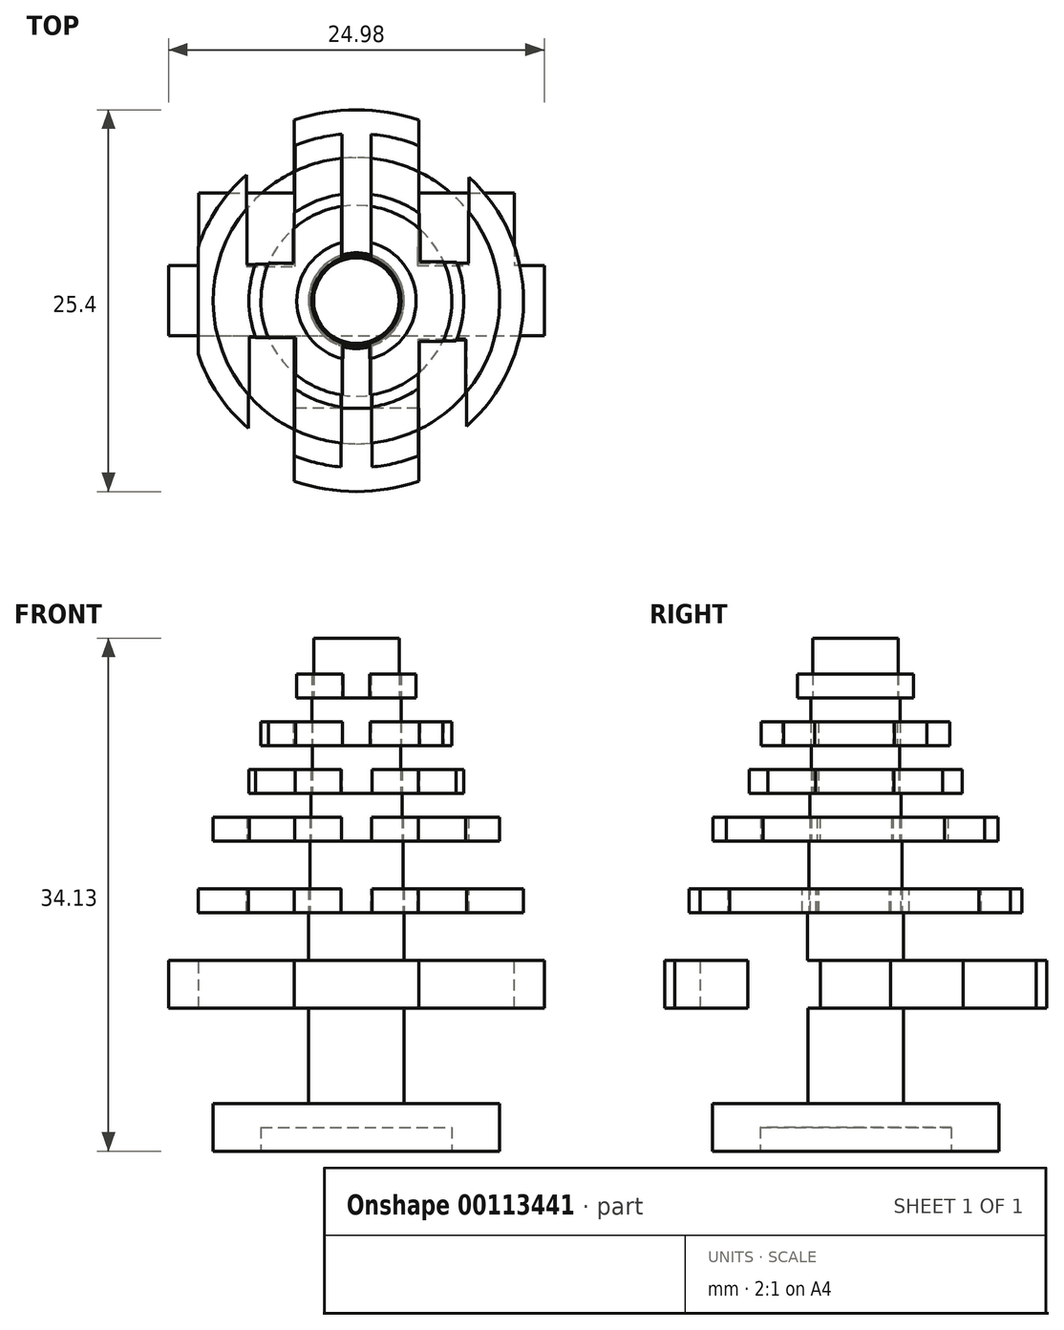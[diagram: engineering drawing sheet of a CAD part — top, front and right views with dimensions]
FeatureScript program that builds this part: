
annotation { "Feature Type Name" : "Feature", "Feature Type Description" : "" }
export const myFeature = defineFeature(function(context is Context, id is Id, definition is map)
    precondition{}
    {
        {
            var Q0;
            Q0=qCreatedBy(makeId("Top.planeOp"),FACE);
            var sketch = newSketch(context, id + "F0", { "sketchPlane" : qUnion([Q0])});
            skCircle(sketch, "E0", {"center": v(0, 0) * mm, "radius": 9.53 * mm});
            skSolve(sketch);
        }
        {
            var Q0;
            Q0=makeQuery(id+"F0.imprint","IMPRINT",FACE,{"disambiguationData":[TD([[makeQuery(id+"F0.imprint","IMPRINT",EDGE,{"derivedFrom":sQuery(id+"F0.wireOp",EDGE,"E0")}),1.0]])]});
            extrude(context, id + "F1", {"entities" : qUnion([Q0]), "depth" : 3.17 * mm});
        }
        {
            var Q0;
            Q0=makeQuery(id+"F1.opExtrude","CAP_FACE",FACE,{"disambiguationData":[OSD([sQuery(id+"F0.wireOp",EDGE,"E0")])],"isStart":false});
            var sketch = newSketch(context, id + "F2", { "sketchPlane" : qUnion([Q0])});
            skCircle(sketch, "E1", {"center": v(0, 0) * mm, "radius": 3.18 * mm});
            skSolve(sketch);
        }
        {
            var Q0;
            Q0=makeQuery(id+"F2.imprint","IMPRINT",FACE,{"disambiguationData":[TD([[makeQuery(id+"F2.imprint","IMPRINT",EDGE,{"derivedFrom":sQuery(id+"F2.wireOp",EDGE,"E1")}),1.0]])]});
            extrude(context, id + "F3", {"entities" : qUnion([Q0]), "depth" : 6.35 * mm});
        }
        {
            var Q0;
            Q0=makeQuery(id+"F1.opExtrude","CAP_FACE",FACE,{"disambiguationData":[OSD([sQuery(id+"F0.wireOp",EDGE,"E0")])],"isStart":true});
            var sketch = newSketch(context, id + "F4", { "sketchPlane" : qUnion([Q0])});
            skCircle(sketch, "E2", {"center": v(0, 0) * mm, "radius": 6.35 * mm});
            skSolve(sketch);
        }
        {
            var Q0;
            Q0=makeQuery(id+"F3.opExtrude","CAP_FACE",FACE,{"disambiguationData":[OSD([sQuery(id+"F2.wireOp",EDGE,"E1")])],"isStart":false});
            var sketch = newSketch(context, id + "F5", { "sketchPlane" : qUnion([Q0])});
            skCircle(sketch, "E3", {"center": v(0, 0) * mm, "radius": 12.7 * mm});
            skSolve(sketch);
        }
        {
            var Q0;
            Q0=makeQuery(id+"F5.imprint","IMPRINT",FACE,{"disambiguationData":[TD([[makeQuery(id+"F5.imprint","IMPRINT",EDGE,{"derivedFrom":makeQuery(id+"F3.opExtrude","CAP_EDGE",EDGE,{"disambiguationData":[OSD([sQuery(id+"F2.wireOp",EDGE,"E1")])],"isStart":false})}),1.0]])]});
            var Q1;
            Q1=makeQuery(id+"F5.imprint","IMPRINT",FACE,{"disambiguationData":[TD([[makeQuery(id+"F5.imprint","IMPRINT",EDGE,{"derivedFrom":sQuery(id+"F5.wireOp",EDGE,"E3")}),1.0]])]});
            extrude(context, id + "F6", {"entities" : qUnion([Q0, Q1]), "operationType" : NewBodyOperationType.ADD, "depth" : 3.17 * mm});
        }
        {
            var Q0;
            Q0=makeQuery(id+"F6.opExtrude","CAP_FACE",FACE,{"disambiguationData":[OSD([sQuery(id+"F5.wireOp",EDGE,"E3")])],"isStart":false});
            var sketch = newSketch(context, id + "F7", { "sketchPlane" : qUnion([Q0])});
            skLineSegment(sketch, "E4", {"start": v(10.49, 7.16) * mm, "end": v(10.49, -7.16) * mm});
            skLineSegment(sketch, "E5", {"start": v(10.49, -2.32) * mm, "end": v(12.49, -2.32) * mm});
            skLineSegment(sketch, "E6", {"start": v(12.49, -2.32) * mm, "end": v(12.49, 2.32) * mm});
            skLineSegment(sketch, "E7", {"start": v(12.49, 2.32) * mm, "end": v(10.49, 2.32) * mm});
            skLineSegment(sketch, "E8", {"start": v(10.49, 2.32) * mm, "end": v(-12.49, 2.32) * mm});
            skLineSegment(sketch, "E9", {"start": v(-12.49, 2.32) * mm, "end": v(-12.49, -2.32) * mm});
            skLineSegment(sketch, "E10", {"start": v(-12.49, -2.32) * mm, "end": v(10.49, -2.32) * mm});
            skLineSegment(sketch, "E11", {"start": v(10.49, -7.16) * mm, "end": v(-10.49, -7.16) * mm});
            skLineSegment(sketch, "E12", {"start": v(-10.49, -7.16) * mm, "end": v(-10.49, 7.16) * mm});
            skLineSegment(sketch, "E13", {"start": v(-10.49, 7.16) * mm, "end": v(10.49, 7.16) * mm});
            skLineSegment(sketch, "E14", {"start": v(-10.49, 2.32) * mm, "end": v(-12.49, 2.32) * mm});
            skLineSegment(sketch, "E15", {"start": v(-10.49, 7.16) * mm, "end": v(-7.31, 7.16) * mm});
            skLineSegment(sketch, "E16", {"start": v(-7.31, 7.16) * mm, "end": v(-7.31, 10.38) * mm});
            skLineSegment(sketch, "E17", {"start": v(-4.14, 12) * mm, "end": v(-4.14, 7.16) * mm});
            skLineSegment(sketch, "E18", {"start": v(-7.31, 7.16) * mm, "end": v(-4.14, 7.16) * mm});
            skLineSegment(sketch, "E19", {"start": v(10.49, 7.16) * mm, "end": v(7.31, 7.16) * mm});
            skLineSegment(sketch, "E20", {"start": v(7.31, 7.16) * mm, "end": v(7.31, 10.38) * mm});
            skLineSegment(sketch, "E21", {"start": v(7.31, 7.16) * mm, "end": v(4.14, 7.16) * mm});
            skLineSegment(sketch, "E22", {"start": v(4.14, 7.16) * mm, "end": v(4.14, 12) * mm});
            skLineSegment(sketch, "E23", {"start": v(-4.14, 7.16) * mm, "end": v(-0.96, 7.16) * mm});
            skLineSegment(sketch, "E24", {"start": v(-0.96, 7.16) * mm, "end": v(-0.96, 12.66) * mm});
            skLineSegment(sketch, "E25", {"start": v(4.14, 7.16) * mm, "end": v(0.96, 7.16) * mm});
            skLineSegment(sketch, "E26", {"start": v(0.96, 7.16) * mm, "end": v(0.96, 12.66) * mm});
            skLineSegment(sketch, "E27", {"start": v(-10.49, -7.16) * mm, "end": v(-7.31, -7.16) * mm});
            skLineSegment(sketch, "E28", {"start": v(-7.31, -7.16) * mm, "end": v(-7.31, -10.38) * mm});
            skLineSegment(sketch, "E29", {"start": v(-7.31, -7.16) * mm, "end": v(-4.14, -7.16) * mm});
            skLineSegment(sketch, "E30", {"start": v(-4.14, -7.16) * mm, "end": v(-4.14, -12) * mm});
            skLineSegment(sketch, "E31", {"start": v(-4.14, -7.16) * mm, "end": v(-0.96, -7.16) * mm});
            skLineSegment(sketch, "E32", {"start": v(-0.96, -7.16) * mm, "end": v(-0.96, -12.66) * mm});
            skLineSegment(sketch, "E33", {"start": v(10.49, -7.16) * mm, "end": v(7.31, -7.16) * mm});
            skLineSegment(sketch, "E34", {"start": v(7.31, -7.16) * mm, "end": v(7.31, -10.38) * mm});
            skLineSegment(sketch, "E35", {"start": v(7.31, -7.16) * mm, "end": v(4.14, -7.16) * mm});
            skLineSegment(sketch, "E36", {"start": v(4.14, -7.16) * mm, "end": v(4.14, -12) * mm});
            skLineSegment(sketch, "E37", {"start": v(4.14, -7.16) * mm, "end": v(0.96, -7.16) * mm});
            skLineSegment(sketch, "E38", {"start": v(0.96, -7.16) * mm, "end": v(0.96, -12.66) * mm});
            skLineSegment(sketch, "E39", {"start": v(-0.96, 7.16) * mm, "end": v(-0.96, 2.32) * mm});
            skLineSegment(sketch, "E40", {"start": v(-0.96, 2.32) * mm, "end": v(-4.14, 2.32) * mm});
            skLineSegment(sketch, "E41", {"start": v(-4.14, 2.32) * mm, "end": v(-4.14, 7.16) * mm});
            skLineSegment(sketch, "E42", {"start": v(-4.14, 2.32) * mm, "end": v(-7.31, 2.32) * mm});
            skLineSegment(sketch, "E43", {"start": v(-7.31, 2.32) * mm, "end": v(-7.31, 7.16) * mm});
            skLineSegment(sketch, "E44", {"start": v(-7.31, 2.32) * mm, "end": v(-10.49, 2.32) * mm});
            skLineSegment(sketch, "E45", {"start": v(0.96, 7.16) * mm, "end": v(0.96, 2.32) * mm});
            skLineSegment(sketch, "E46", {"start": v(0.96, 2.32) * mm, "end": v(4.14, 2.32) * mm});
            skLineSegment(sketch, "E47", {"start": v(4.14, 2.32) * mm, "end": v(4.14, 7.16) * mm});
            skLineSegment(sketch, "E48", {"start": v(4.14, 2.32) * mm, "end": v(7.31, 2.32) * mm});
            skLineSegment(sketch, "E49", {"start": v(7.31, 2.32) * mm, "end": v(7.31, 7.16) * mm});
            skLineSegment(sketch, "E50", {"start": v(7.31, 2.32) * mm, "end": v(10.49, 2.32) * mm});
            skLineSegment(sketch, "E51", {"start": v(7.31, -7.16) * mm, "end": v(7.31, -2.32) * mm});
            skLineSegment(sketch, "E52", {"start": v(4.14, -7.16) * mm, "end": v(4.14, -2.32) * mm});
            skLineSegment(sketch, "E53", {"start": v(0.96, -7.16) * mm, "end": v(0.96, -2.32) * mm});
            skLineSegment(sketch, "E54", {"start": v(-0.96, -7.16) * mm, "end": v(-0.96, -2.32) * mm});
            skLineSegment(sketch, "E55", {"start": v(-4.14, -7.16) * mm, "end": v(-4.14, -2.32) * mm});
            skLineSegment(sketch, "E56", {"start": v(-7.31, -7.16) * mm, "end": v(-7.31, -2.32) * mm});
            skSolve(sketch);
        }
        {
            var Q0;
            {var subQ1=sQuery(id+"F7.wireOp",EDGE,"E9");Q0=makeQuery(id+"F7.imprint","IMPRINT",FACE,{"disambiguationData":[TD([[makeQuery(id+"F7.imprint","IMPRINT",EDGE,{"derivedFrom":subQ1}),-1.0]])]});}
            var Q1;
            {var subQ3=sQuery(id+"F7.wireOp",EDGE,"E14");Q1=makeQuery(id+"F7.imprint","IMPRINT",FACE,{"disambiguationData":[TD([[makeQuery(id+"F7.imprint","IMPRINT",EDGE,{"derivedFrom":subQ3}),-1.0]])]});}
            var Q2;
            {var subQ1=sQuery(id+"F7.wireOp",EDGE,"E12");var subQ3=sQuery(id+"F7.wireOp",EDGE,"E10");var subQ5=makeQuery(id+"F7.imprint","INTERSECT",VERTEX,{"derivedFrom":[subQ3,subQ1]});Q2=makeQuery(id+"F7.imprint","IMPRINT",FACE,{"disambiguationData":[TD([[makeQuery(id+"F7.imprint","IMPRINT",EDGE,{"disambiguationData":[TD([[subQ5,1.0]])],"derivedFrom":subQ3}),-1.0]])]});}
            var Q3;
            {var subQ2=sQuery(id+"F7.wireOp",EDGE,"E28");Q3=makeQuery(id+"F7.imprint","IMPRINT",FACE,{"disambiguationData":[TD([[makeQuery(id+"F7.imprint","IMPRINT",EDGE,{"derivedFrom":subQ2}),1.0]])]});}
            var Q4;
            Q4=makeQuery(id+"F7.imprint","IMPRINT",FACE,{"disambiguationData":[TD([[makeQuery(id+"F7.imprint","IMPRINT",EDGE,{"derivedFrom":sQuery(id+"F7.wireOp",EDGE,"E29")}),1.0]])]});
            var Q5;
            Q5=makeQuery(id+"F7.imprint","IMPRINT",FACE,{"disambiguationData":[TD([[makeQuery(id+"F7.imprint","IMPRINT",EDGE,{"derivedFrom":sQuery(id+"F7.wireOp",EDGE,"E18")}),-1.0]])]});
            var Q6;
            {var subQ2=sQuery(id+"F7.wireOp",EDGE,"E16");Q6=makeQuery(id+"F7.imprint","IMPRINT",FACE,{"disambiguationData":[TD([[makeQuery(id+"F7.imprint","IMPRINT",EDGE,{"derivedFrom":subQ2}),-1.0]])]});}
            var Q7;
            Q7=makeQuery(id+"F7.imprint","IMPRINT",FACE,{"disambiguationData":[TD([[makeQuery(id+"F7.imprint","IMPRINT",EDGE,{"derivedFrom":sQuery(id+"F7.wireOp",EDGE,"E13")}),1.0]])]});
            var Q8;
            Q8=makeQuery(id+"F7.imprint","IMPRINT",FACE,{"disambiguationData":[TD([[makeQuery(id+"F7.imprint","IMPRINT",EDGE,{"derivedFrom":sQuery(id+"F7.wireOp",EDGE,"E8")}),-1.0]])]});
            var Q9;
            Q9=makeQuery(id+"F7.imprint","IMPRINT",FACE,{"disambiguationData":[TD([[makeQuery(id+"F7.imprint","IMPRINT",EDGE,{"derivedFrom":sQuery(id+"F7.wireOp",EDGE,"E11")}),-1.0]])]});
            var Q10;
            Q10=makeQuery(id+"F7.imprint","IMPRINT",FACE,{"disambiguationData":[TD([[makeQuery(id+"F7.imprint","IMPRINT",EDGE,{"derivedFrom":sQuery(id+"F7.wireOp",EDGE,"E11")}),1.0]])]});
            var Q11;
            {var subQ2=sQuery(id+"F7.wireOp",EDGE,"E34");Q11=makeQuery(id+"F7.imprint","IMPRINT",FACE,{"disambiguationData":[TD([[makeQuery(id+"F7.imprint","IMPRINT",EDGE,{"derivedFrom":subQ2}),-1.0]])]});}
            var Q12;
            Q12=makeQuery(id+"F7.imprint","IMPRINT",FACE,{"disambiguationData":[TD([[makeQuery(id+"F7.imprint","IMPRINT",EDGE,{"derivedFrom":sQuery(id+"F7.wireOp",EDGE,"E35")}),-1.0]])]});
            var Q13;
            {var subQ1=sQuery(id+"F7.wireOp",EDGE,"E5");Q13=makeQuery(id+"F7.imprint","IMPRINT",FACE,{"disambiguationData":[TD([[makeQuery(id+"F7.imprint","IMPRINT",EDGE,{"derivedFrom":subQ1}),-1.0]])]});}
            var Q14;
            {var subQ0=sQuery(id+"F7.wireOp",EDGE,"E7");Q14=makeQuery(id+"F7.imprint","IMPRINT",FACE,{"disambiguationData":[TD([[makeQuery(id+"F7.imprint","IMPRINT",EDGE,{"derivedFrom":subQ0}),-1.0]])]});}
            var Q15;
            Q15=makeQuery(id+"F7.imprint","IMPRINT",FACE,{"disambiguationData":[TD([[makeQuery(id+"F7.imprint","IMPRINT",EDGE,{"derivedFrom":sQuery(id+"F7.wireOp",EDGE,"E21")}),1.0]])]});
            var Q16;
            {var subQ2=sQuery(id+"F7.wireOp",EDGE,"E20");Q16=makeQuery(id+"F7.imprint","IMPRINT",FACE,{"disambiguationData":[TD([[makeQuery(id+"F7.imprint","IMPRINT",EDGE,{"derivedFrom":subQ2}),1.0]])]});}
            var Q17;
            {var subQ1=sQuery(id+"F7.wireOp",EDGE,"E6");Q17=makeQuery(id+"F7.imprint","IMPRINT",FACE,{"disambiguationData":[TD([[makeQuery(id+"F7.imprint","IMPRINT",EDGE,{"derivedFrom":subQ1}),-1.0]])]});}
            extrude(context, id + "F8", {"entities" : qUnion([Q0, Q1, Q2, Q3, Q4, Q5, Q6, Q7, Q8, Q9, Q10, Q11, Q12, Q13, Q14, Q15, Q16, Q17]), "operationType" : NewBodyOperationType.REMOVE, "oppositeDirection" : true, "depth" : 3.17 * mm});
        }
        {
            var Q0;
            Q0=makeQuery(id+"F7.imprint","IMPRINT",FACE,{"disambiguationData":[TD([[makeQuery(id+"F7.imprint","IMPRINT",EDGE,{"derivedFrom":sQuery(id+"F7.wireOp",EDGE,"E8")}),1.0]])]});
            var sketch = newSketch(context, id + "F9", { "sketchPlane" : qUnion([Q0])});
            skCircle(sketch, "E57", {"center": v(0, 0) * mm, "radius": 3.18 * mm});
            skSolve(sketch);
        }
        {
            var Q0;
            Q0=qSketchRegion(id+"F9",true);
            extrude(context, id + "F10", {"entities" : qUnion([Q0]), "operationType" : NewBodyOperationType.ADD, "depth" : 3.17 * mm});
        }
        {
            var Q0;
            Q0=makeQuery(id+"F10.opExtrude","CAP_FACE",FACE,{"disambiguationData":[OSD([sQuery(id+"F9.wireOp",EDGE,"E57")])],"isStart":false});
            var sketch = newSketch(context, id + "F11", { "sketchPlane" : qUnion([Q0])});
            skCircle(sketch, "E58", {"center": v(0, 0) * mm, "radius": 11.11 * mm});
            skSolve(sketch);
        }
        {
            var Q0;
            Q0=makeQuery(id+"F11.imprint","IMPRINT",FACE,{"disambiguationData":[TD([[makeQuery(id+"F11.imprint","IMPRINT",EDGE,{"derivedFrom":sQuery(id+"F11.wireOp",EDGE,"E58")}),1.0]])]});
            extrude(context, id + "F12", {"entities" : qUnion([Q0]), "depth" : 1.59 * mm});
        }
        {
            var Q0;
            Q0=makeQuery(id+"F12.opExtrude","CAP_FACE",FACE,{"disambiguationData":[OSD([sQuery(id+"F9.wireOp",EDGE,"E57"),sQuery(id+"F11.wireOp",EDGE,"E58")])],"isStart":false});
            var sketch = newSketch(context, id + "F13", { "sketchPlane" : qUnion([Q0])});
            skLineSegment(sketch, "E59", {"start": v(-0.97, 3.03) * mm, "end": v(-0.97, 11.07) * mm});
            skLineSegment(sketch, "E60", {"start": v(-0.97, 11.07) * mm, "end": v(0.97, 11.07) * mm});
            skLineSegment(sketch, "E61", {"start": v(0.97, 11.07) * mm, "end": v(0.97, 3.03) * mm});
            skLineSegment(sketch, "E62", {"start": v(0.97, 3.03) * mm, "end": v(-0.97, 3.03) * mm});
            skLineSegment(sketch, "E63", {"start": v(4.06, 2.35) * mm, "end": v(7.5, 2.35) * mm});
            skLineSegment(sketch, "E64", {"start": v(7.5, 2.35) * mm, "end": v(7.5, 8.2) * mm});
            skLineSegment(sketch, "E65", {"start": v(7.5, 8.2) * mm, "end": v(4.16, 10.3) * mm});
            skLineSegment(sketch, "E66", {"start": v(4.16, 10.3) * mm, "end": v(4.06, 2.35) * mm});
            skLineSegment(sketch, "E67", {"start": v(10.59, 3.37) * mm, "end": v(10.59, -3.37) * mm});
            skLineSegment(sketch, "E68", {"start": v(-10.53, 3.55) * mm, "end": v(-10.53, -3.55) * mm});
            skLineSegment(sketch, "E69", {"start": v(-7.31, 8.37) * mm, "end": v(-7.31, 2.26) * mm});
            skLineSegment(sketch, "E70", {"start": v(-7.31, 2.26) * mm, "end": v(-4.08, 2.26) * mm});
            skLineSegment(sketch, "E71", {"start": v(-4.08, 2.26) * mm, "end": v(-4.08, 10.34) * mm});
            skLineSegment(sketch, "E72", {"start": v(-4.08, 10.34) * mm, "end": v(-7.31, 8.37) * mm});
            skLineSegment(sketch, "E73", {"start": v(-7.17, -2.44) * mm, "end": v(-7.17, -8.49) * mm});
            skLineSegment(sketch, "E74", {"start": v(-7.17, -8.49) * mm, "end": v(-4.13, -10.32) * mm});
            skLineSegment(sketch, "E75", {"start": v(-4.13, -10.32) * mm, "end": v(-4.13, -2.48) * mm});
            skLineSegment(sketch, "E76", {"start": v(-4.13, -2.48) * mm, "end": v(-7.17, -2.44) * mm});
            skLineSegment(sketch, "E77", {"start": v(-1.04, -2.53) * mm, "end": v(-1.04, -11.06) * mm});
            skLineSegment(sketch, "E78", {"start": v(-1.04, -11.06) * mm, "end": v(1.04, -11.06) * mm});
            skLineSegment(sketch, "E79", {"start": v(1.04, -11.06) * mm, "end": v(1.04, -3) * mm});
            skLineSegment(sketch, "E80", {"start": v(1.04, -3) * mm, "end": v(-1.04, -3) * mm});
            skLineSegment(sketch, "E81", {"start": v(4.11, -10.32) * mm, "end": v(4.11, -2.61) * mm});
            skLineSegment(sketch, "E82", {"start": v(4.11, -2.61) * mm, "end": v(7.32, -2.61) * mm});
            skLineSegment(sketch, "E83", {"start": v(7.32, -2.61) * mm, "end": v(7.32, -8.36) * mm});
            skLineSegment(sketch, "E84", {"start": v(7.32, -8.36) * mm, "end": v(4.11, -10.32) * mm});
            skSolve(sketch);
        }
        {
            var Q0;
            {var subQ1=sQuery(id+"F13.wireOp",EDGE,"E78");Q0=makeQuery(id+"F13.imprint","IMPRINT",FACE,{"disambiguationData":[TD([[makeQuery(id+"F13.imprint","IMPRINT",EDGE,{"derivedFrom":subQ1}),1.0]])]});}
            var Q1;
            Q1=makeQuery(id+"F13.imprint","IMPRINT",FACE,{"disambiguationData":[TD([[makeQuery(id+"F13.imprint","IMPRINT",EDGE,{"derivedFrom":sQuery(id+"F13.wireOp",EDGE,"E81")}),-1.0]])]});
            var Q2;
            Q2=makeQuery(id+"F13.imprint","IMPRINT",FACE,{"disambiguationData":[TD([[makeQuery(id+"F13.imprint","IMPRINT",EDGE,{"derivedFrom":sQuery(id+"F13.wireOp",EDGE,"E73")}),1.0]])]});
            var Q3;
            {var subQ1=sQuery(id+"F13.wireOp",EDGE,"E68");Q3=makeQuery(id+"F13.imprint","IMPRINT",FACE,{"disambiguationData":[TD([[makeQuery(id+"F13.imprint","IMPRINT",EDGE,{"derivedFrom":subQ1}),-1.0]])]});}
            var Q4;
            Q4=makeQuery(id+"F13.imprint","IMPRINT",FACE,{"disambiguationData":[TD([[makeQuery(id+"F13.imprint","IMPRINT",EDGE,{"derivedFrom":sQuery(id+"F13.wireOp",EDGE,"E69")}),1.0]])]});
            var Q5;
            {var subQ3=sQuery(id+"F13.wireOp",EDGE,"E59");Q5=makeQuery(id+"F13.imprint","IMPRINT",FACE,{"disambiguationData":[TD([[makeQuery(id+"F13.imprint","IMPRINT",EDGE,{"derivedFrom":subQ3}),-1.0]])]});}
            var Q6;
            Q6=makeQuery(id+"F13.imprint","IMPRINT",FACE,{"disambiguationData":[TD([[makeQuery(id+"F13.imprint","IMPRINT",EDGE,{"derivedFrom":sQuery(id+"F13.wireOp",EDGE,"E63")}),1.0]])]});
            var Q7;
            {var subQ1=sQuery(id+"F13.wireOp",EDGE,"E65");Q7=makeQuery(id+"F13.imprint","IMPRINT",FACE,{"disambiguationData":[TD([[makeQuery(id+"F13.imprint","IMPRINT",EDGE,{"derivedFrom":subQ1}),-1.0]])]});}
            var Q8;
            {var subQ1=sQuery(id+"F13.wireOp",EDGE,"E78");Q8=makeQuery(id+"F13.imprint","IMPRINT",FACE,{"disambiguationData":[TD([[makeQuery(id+"F13.imprint","IMPRINT",EDGE,{"derivedFrom":subQ1}),-1.0]])]});}
            var Q9;
            {var subQ1=sQuery(id+"F13.wireOp",EDGE,"E84");Q9=makeQuery(id+"F13.imprint","IMPRINT",FACE,{"disambiguationData":[TD([[makeQuery(id+"F13.imprint","IMPRINT",EDGE,{"derivedFrom":subQ1}),1.0]])]});}
            var Q10;
            {var subQ1=sQuery(id+"F13.wireOp",EDGE,"E72");Q10=makeQuery(id+"F13.imprint","IMPRINT",FACE,{"disambiguationData":[TD([[makeQuery(id+"F13.imprint","IMPRINT",EDGE,{"derivedFrom":subQ1}),-1.0]])]});}
            var Q11;
            {var subQ1=sQuery(id+"F13.wireOp",EDGE,"E60");Q11=makeQuery(id+"F13.imprint","IMPRINT",FACE,{"disambiguationData":[TD([[makeQuery(id+"F13.imprint","IMPRINT",EDGE,{"derivedFrom":subQ1}),1.0]])]});}
            extrude(context, id + "F14", {"entities" : qUnion([Q0, Q1, Q2, Q3, Q4, Q5, Q6, Q7, Q8, Q9, Q10, Q11]), "operationType" : NewBodyOperationType.REMOVE, "oppositeDirection" : true, "depth" : 1.59 * mm});
        }
        {
            var Q0;
            Q0=makeQuery(id+"F4.imprint","IMPRINT",FACE,{"disambiguationData":[TD([[makeQuery(id+"F4.imprint","IMPRINT",EDGE,{"derivedFrom":sQuery(id+"F4.wireOp",EDGE,"E2")}),1.0]])]});
            extrude(context, id + "F15", {"entities" : qUnion([Q0]), "operationType" : NewBodyOperationType.REMOVE, "oppositeDirection" : true, "depth" : 1.59 * mm});
        }
        {
            var Q0;
            Q0=makeQuery(id+"F10.opExtrude","CAP_FACE",FACE,{"disambiguationData":[OSD([sQuery(id+"F9.wireOp",EDGE,"E57")])],"isStart":false});
            var sketch = newSketch(context, id + "F16", { "sketchPlane" : qUnion([Q0])});
            skCircle(sketch, "E85", {"center": v(0, 0) * mm, "radius": 3.1 * mm});
            skSolve(sketch);
        }
        {
            var Q0;
            Q0=makeQuery(id+"F16.imprint","IMPRINT",FACE,{"disambiguationData":[TD([[makeQuery(id+"F16.imprint","IMPRINT",EDGE,{"derivedFrom":sQuery(id+"F16.wireOp",EDGE,"E85")}),1.0]])]});
            extrude(context, id + "F17", {"entities" : qUnion([Q0]), "depth" : 4.76 * mm});
        }
        {
            var Q0;
            {var subQ0=sQuery(id+"F11.wireOp",EDGE,"E58");Q0=makeQuery(id+"F14.boolean.opBoolean","SPLIT",FACE,{"disambiguationData":[TD([makeQuery(id+"F14.opExtrude","SWEPT_FACE",FACE,{"disambiguationData":[OSD([sQuery(id+"F13.wireOp",EDGE,"E74")])]})])],"derivedFrom":makeQuery(id+"F12.opExtrude","CAP_FACE",FACE,{"disambiguationData":[OSD([sQuery(id+"F9.wireOp",EDGE,"E57"),subQ0])],"isStart":false})});}
            extrude(context, id + "F18", {"entities" : qUnion([Q0]), "operationType" : NewBodyOperationType.REMOVE, "oppositeDirection" : true, "depth" : 25.4 * mm});
        }
        {
            var Q0;
            Q0=makeQuery(id+"F17.opExtrude","CAP_FACE",FACE,{"disambiguationData":[OSD([sQuery(id+"F16.wireOp",EDGE,"E85")])],"isStart":false});
            var sketch = newSketch(context, id + "F19", { "sketchPlane" : qUnion([Q0])});
            skCircle(sketch, "E86", {"center": v(0, 0) * mm, "radius": 9.53 * mm});
            skLineSegment(sketch, "E87", {"start": v(-0.98, 9.47) * mm, "end": v(-0.98, 2.94) * mm});
            skLineSegment(sketch, "E88", {"start": v(-0.98, 2.94) * mm, "end": v(0.98, 2.94) * mm});
            skLineSegment(sketch, "E89", {"start": v(0.98, 2.94) * mm, "end": v(0.98, 9.47) * mm});
            skLineSegment(sketch, "E90", {"start": v(0.98, 9.47) * mm, "end": v(-0.98, 9.47) * mm});
            skLineSegment(sketch, "E91", {"start": v(4.15, 8.57) * mm, "end": v(4.15, 2.48) * mm});
            skLineSegment(sketch, "E92", {"start": v(4.15, 2.48) * mm, "end": v(7.46, 2.48) * mm});
            skLineSegment(sketch, "E93", {"start": v(7.46, 2.48) * mm, "end": v(7.46, 5.92) * mm});
            skLineSegment(sketch, "E94", {"start": v(-4.1, 8.6) * mm, "end": v(-4.1, 2.39) * mm});
            skLineSegment(sketch, "E95", {"start": v(-4.1, 2.39) * mm, "end": v(-7.28, 2.39) * mm});
            skLineSegment(sketch, "E96", {"start": v(-7.28, 2.39) * mm, "end": v(-7.28, 6.14) * mm});
            skLineSegment(sketch, "E97", {"start": v(-7.12, -6.32) * mm, "end": v(-7.12, -2.38) * mm});
            skLineSegment(sketch, "E98", {"start": v(-7.12, -2.38) * mm, "end": v(-4.11, -2.38) * mm});
            skLineSegment(sketch, "E99", {"start": v(-4.11, -2.38) * mm, "end": v(-4.11, -8.6) * mm});
            skLineSegment(sketch, "E100", {"start": v(-1, -9.47) * mm, "end": v(-1, -2.93) * mm});
            skLineSegment(sketch, "E101", {"start": v(-1, -2.93) * mm, "end": v(1, -2.93) * mm});
            skLineSegment(sketch, "E102", {"start": v(1, -2.93) * mm, "end": v(1, -9.47) * mm});
            skLineSegment(sketch, "E103", {"start": v(4.11, -8.6) * mm, "end": v(4.11, -2.57) * mm});
            skLineSegment(sketch, "E104", {"start": v(4.11, -2.57) * mm, "end": v(7.27, -2.57) * mm});
            skLineSegment(sketch, "E105", {"start": v(7.27, -2.57) * mm, "end": v(7.27, -6.15) * mm});
            skSolve(sketch);
        }
        {
            var Q0;
            {var subQ5=sQuery(id+"F19.wireOp",EDGE,"E89");Q0=makeQuery(id+"F19.imprint","IMPRINT",FACE,{"disambiguationData":[TD([[makeQuery(id+"F19.imprint","IMPRINT",EDGE,{"derivedFrom":subQ5}),-1.0]])]});}
            var Q1;
            {var subQ5=sQuery(id+"F19.wireOp",EDGE,"E87");Q1=makeQuery(id+"F19.imprint","IMPRINT",FACE,{"disambiguationData":[TD([[makeQuery(id+"F19.imprint","IMPRINT",EDGE,{"derivedFrom":subQ5}),-1.0]])]});}
            extrude(context, id + "F20", {"entities" : qUnion([Q0, Q1]), "depth" : 1.59 * mm});
        }
        {
            var Q0;
            Q0=makeQuery(id+"F17.opExtrude","CAP_FACE",FACE,{"disambiguationData":[OSD([sQuery(id+"F16.wireOp",EDGE,"E85")])],"isStart":false});
            var sketch = newSketch(context, id + "F21", { "sketchPlane" : qUnion([Q0])});
            skCircle(sketch, "E106", {"center": v(0, 0) * mm, "radius": 3.04 * mm});
            skSolve(sketch);
        }
        {
            var Q0;
            Q0=makeQuery(id+"F21.imprint","IMPRINT",FACE,{"disambiguationData":[TD([[makeQuery(id+"F21.imprint","IMPRINT",EDGE,{"derivedFrom":sQuery(id+"F21.wireOp",EDGE,"E106")}),1.0]])]});
            extrude(context, id + "F22", {"entities" : qUnion([Q0]), "operationType" : NewBodyOperationType.ADD, "depth" : 3.17 * mm});
        }
        {
            var Q0;
            Q0=makeQuery(id+"F22.opExtrude","CAP_FACE",FACE,{"disambiguationData":[OSD([sQuery(id+"F21.wireOp",EDGE,"E106")])],"isStart":false});
            var sketch = newSketch(context, id + "F23", { "sketchPlane" : qUnion([Q0])});
            skCircle(sketch, "E107", {"center": v(0, 0) * mm, "radius": 7.14 * mm});
            skLineSegment(sketch, "E108", {"start": v(-4.14, 5.82) * mm, "end": v(-4.14, 2.42) * mm});
            skLineSegment(sketch, "E109", {"start": v(-4.14, 2.42) * mm, "end": v(-6.72, 2.42) * mm});
            skLineSegment(sketch, "E110", {"start": v(-0.97, 7.08) * mm, "end": v(-0.97, 2.88) * mm});
            skLineSegment(sketch, "E111", {"start": v(-0.97, 2.88) * mm, "end": v(0.97, 2.88) * mm});
            skLineSegment(sketch, "E112", {"start": v(0.97, 2.88) * mm, "end": v(0.97, 7.08) * mm});
            skLineSegment(sketch, "E113", {"start": v(4.18, 5.8) * mm, "end": v(4.18, 2.55) * mm});
            skLineSegment(sketch, "E114", {"start": v(4.18, 2.55) * mm, "end": v(6.67, 2.55) * mm});
            skLineSegment(sketch, "E115", {"start": v(4.13, -5.83) * mm, "end": v(4.13, -2.67) * mm});
            skLineSegment(sketch, "E116", {"start": v(4.13, -2.67) * mm, "end": v(6.63, -2.67) * mm});
            skLineSegment(sketch, "E117", {"start": v(1.03, -7.07) * mm, "end": v(1.03, -2.86) * mm});
            skLineSegment(sketch, "E118", {"start": v(1.03, -2.86) * mm, "end": v(-1.03, -2.86) * mm});
            skLineSegment(sketch, "E119", {"start": v(-1.03, -2.86) * mm, "end": v(-1.03, -7.07) * mm});
            skLineSegment(sketch, "E120", {"start": v(-4.08, -5.86) * mm, "end": v(-4.08, -2.45) * mm});
            skLineSegment(sketch, "E121", {"start": v(-4.08, -2.45) * mm, "end": v(-6.71, -2.45) * mm});
            skSolve(sketch);
        }
        {
            var Q0;
            {var subQ0=sQuery(id+"F23.wireOp",EDGE,"E108");Q0=makeQuery(id+"F23.imprint","IMPRINT",FACE,{"disambiguationData":[TD([[makeQuery(id+"F23.imprint","IMPRINT",EDGE,{"derivedFrom":subQ0}),1.0]])]});}
            var Q1;
            {var subQ0=sQuery(id+"F23.wireOp",EDGE,"E112");Q1=makeQuery(id+"F23.imprint","IMPRINT",FACE,{"disambiguationData":[TD([[makeQuery(id+"F23.imprint","IMPRINT",EDGE,{"derivedFrom":subQ0}),-1.0]])]});}
            extrude(context, id + "F24", {"entities" : qUnion([Q0, Q1]), "depth" : 1.59 * mm});
        }
        {
            var Q0;
            Q0=makeQuery(id+"F22.opExtrude","CAP_FACE",FACE,{"disambiguationData":[OSD([sQuery(id+"F21.wireOp",EDGE,"E106")])],"isStart":false});
            var sketch = newSketch(context, id + "F25", { "sketchPlane" : qUnion([Q0])});
            skCircle(sketch, "E122", {"center": v(0, 0) * mm, "radius": 2.94 * mm});
            skSolve(sketch);
        }
        {
            var Q0;
            Q0=makeQuery(id+"F25.imprint","IMPRINT",FACE,{"disambiguationData":[TD([[makeQuery(id+"F25.imprint","IMPRINT",EDGE,{"derivedFrom":sQuery(id+"F25.wireOp",EDGE,"E122")}),1.0]])]});
            extrude(context, id + "F26", {"entities" : qUnion([Q0]), "operationType" : NewBodyOperationType.ADD, "depth" : 3.17 * mm});
        }
        {
            var Q0;
            Q0=makeQuery(id+"F26.opExtrude","CAP_FACE",FACE,{"disambiguationData":[OSD([sQuery(id+"F25.wireOp",EDGE,"E122")])],"isStart":false});
            var sketch = newSketch(context, id + "F27", { "sketchPlane" : qUnion([Q0])});
            skCircle(sketch, "E123", {"center": v(0, 0) * mm, "radius": 6.35 * mm});
            skLineSegment(sketch, "E124", {"start": v(-0.98, 6.27) * mm, "end": v(-0.98, 2.77) * mm});
            skLineSegment(sketch, "E125", {"start": v(-0.98, 2.77) * mm, "end": v(0.98, 2.77) * mm});
            skLineSegment(sketch, "E126", {"start": v(0.98, 2.77) * mm, "end": v(0.98, 6.27) * mm});
            skLineSegment(sketch, "E127", {"start": v(4.23, 4.73) * mm, "end": v(4.23, 2.58) * mm});
            skLineSegment(sketch, "E128", {"start": v(4.23, 2.58) * mm, "end": v(5.8, 2.58) * mm});
            skLineSegment(sketch, "E129", {"start": v(5.85, -2.7) * mm, "end": v(4.19, -2.7) * mm});
            skLineSegment(sketch, "E130", {"start": v(4.19, -2.7) * mm, "end": v(4.19, -4.99) * mm});
            skLineSegment(sketch, "E131", {"start": v(-0.92, -6.28) * mm, "end": v(-0.92, -2.8) * mm});
            skLineSegment(sketch, "E132", {"start": v(-0.92, -2.8) * mm, "end": v(0.92, -2.8) * mm});
            skLineSegment(sketch, "E133", {"start": v(0.92, -2.8) * mm, "end": v(0.92, -6.28) * mm});
            skLineSegment(sketch, "E134", {"start": v(-4.04, -4.9) * mm, "end": v(-4.04, -2.46) * mm});
            skLineSegment(sketch, "E135", {"start": v(-4.04, -2.46) * mm, "end": v(-5.85, -2.46) * mm});
            skLineSegment(sketch, "E136", {"start": v(-5.84, 2.49) * mm, "end": v(-4.19, 2.49) * mm});
            skLineSegment(sketch, "E137", {"start": v(-4.19, 2.49) * mm, "end": v(-4.19, 4.78) * mm});
            skSolve(sketch);
        }
        {
            var Q0;
            {var subQ0=sQuery(id+"F27.wireOp",EDGE,"E124");Q0=makeQuery(id+"F27.imprint","IMPRINT",FACE,{"disambiguationData":[TD([[makeQuery(id+"F27.imprint","IMPRINT",EDGE,{"derivedFrom":subQ0}),-1.0]])]});}
            var Q1;
            {var subQ0=sQuery(id+"F27.wireOp",EDGE,"E126");Q1=makeQuery(id+"F27.imprint","IMPRINT",FACE,{"disambiguationData":[TD([[makeQuery(id+"F27.imprint","IMPRINT",EDGE,{"derivedFrom":subQ0}),-1.0]])]});}
            extrude(context, id + "F28", {"entities" : qUnion([Q0, Q1]), "depth" : 1.59 * mm});
        }
        {
            var Q0;
            Q0=makeQuery(id+"F26.opExtrude","CAP_FACE",FACE,{"disambiguationData":[OSD([sQuery(id+"F25.wireOp",EDGE,"E122")])],"isStart":false});
            var sketch = newSketch(context, id + "F29", { "sketchPlane" : qUnion([Q0])});
            skCircle(sketch, "E138", {"center": v(0, 0) * mm, "radius": 2.96 * mm});
            skSolve(sketch);
        }
        {
            var Q0;
            Q0=qSketchRegion(id+"F29",true);
            extrude(context, id + "F30", {"entities" : qUnion([Q0]), "depth" : 3.17 * mm});
        }
        {
            var Q0;
            Q0=makeQuery(id+"F30.opExtrude","CAP_FACE",FACE,{"disambiguationData":[OSD([sQuery(id+"F29.wireOp",EDGE,"E138")])],"isStart":false});
            var sketch = newSketch(context, id + "F31", { "sketchPlane" : qUnion([Q0])});
            skCircle(sketch, "E139", {"center": v(0, 0) * mm, "radius": 3.97 * mm});
            skLineSegment(sketch, "E140", {"start": v(-0.98, 3.85) * mm, "end": v(-0.98, 2.8) * mm});
            skLineSegment(sketch, "E141", {"start": v(-0.98, 2.8) * mm, "end": v(0.98, 2.8) * mm});
            skLineSegment(sketch, "E142", {"start": v(0.98, 2.8) * mm, "end": v(0.98, 3.85) * mm});
            skLineSegment(sketch, "E143", {"start": v(-0.88, -3.87) * mm, "end": v(-0.88, -2.83) * mm});
            skLineSegment(sketch, "E144", {"start": v(-0.88, -2.83) * mm, "end": v(0.88, -2.83) * mm});
            skLineSegment(sketch, "E145", {"start": v(0.88, -2.83) * mm, "end": v(0.88, -3.87) * mm});
            skSolve(sketch);
        }
        {
            var Q0;
            {var subQ0=sQuery(id+"F31.wireOp",EDGE,"E142");Q0=makeQuery(id+"F31.imprint","IMPRINT",FACE,{"disambiguationData":[TD([[makeQuery(id+"F31.imprint","IMPRINT",EDGE,{"derivedFrom":subQ0}),-1.0]])]});}
            var Q1;
            {var subQ0=sQuery(id+"F31.wireOp",EDGE,"E140");Q1=makeQuery(id+"F31.imprint","IMPRINT",FACE,{"disambiguationData":[TD([[makeQuery(id+"F31.imprint","IMPRINT",EDGE,{"derivedFrom":subQ0}),-1.0]])]});}
            extrude(context, id + "F32", {"entities" : qUnion([Q0, Q1]), "depth" : 1.59 * mm});
        }
        {
            var Q0;
            Q0=makeQuery(id+"F30.opExtrude","CAP_FACE",FACE,{"disambiguationData":[OSD([sQuery(id+"F29.wireOp",EDGE,"E138")])],"isStart":false});
            var sketch = newSketch(context, id + "F33", { "sketchPlane" : qUnion([Q0])});
            skCircle(sketch, "E146", {"center": v(0, 0) * mm, "radius": 2.85 * mm});
            skSolve(sketch);
        }
        {
            var Q0;
            Q0=makeQuery(id+"F33.imprint","IMPRINT",FACE,{"disambiguationData":[TD([[makeQuery(id+"F33.imprint","IMPRINT",EDGE,{"derivedFrom":sQuery(id+"F33.wireOp",EDGE,"E146")}),1.0]])]});
            extrude(context, id + "F34", {"entities" : qUnion([Q0]), "operationType" : NewBodyOperationType.ADD, "depth" : 3.97 * mm});
        }
    });
